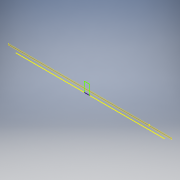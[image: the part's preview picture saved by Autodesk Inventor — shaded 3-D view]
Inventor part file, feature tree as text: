
AUTODESK INVENTOR PART (.ipt)
format: ipt  version: 2019 (Build 230136000, 136)  size: 148,480 bytes
history: native  units: mm
features: extrude x4, sketch x4, reference x4, other x4, fillet x2, plane x1, helix x1
ambient origin geometry x8: Origin, YZ Plane, XZ Plane, XY Plane, X Axis, Y Axis, Z Axis, Center Point
bodies: Solid1 (feature_tree)
feature tree (20):
  plane  "Work Plane1"
  extrude  "Extrusion1"  Depth=2.0mm
  fillet  "Fillet1"  Radius=6.2mm
  extrude  "Extrusion2"  Depth=4.0mm TaperAngle=0.0deg
  extrude  "Extrusion3"  Depth=4.0mm TaperAngle=0.0deg
  extrude  "Extrusion4"  [1 undecoded]
  fillet  "Fillet2"  [1 undecoded]
  sketch  "Sketch1"  dims[d0=4.0mm d1=0.0mm d2=2.0mm d3=6.2mm]
  reference  "Reference1"
  sketch  "Sketch2"  dims[d4=6.0mm d5=4.0mm d6=0.0mm]
  reference  "Reference2"
  sketch  "Sketch3"  dims[d7=4.0mm d8=0.0mm d9=4.0mm d10=0.0mm]
  reference  "Reference3"
  reference  "Reference4"
  sketch  "Sketch4"  dims[d11=2.0mm]
  other  "<userpath>\Documents\CAD Files\Helix DLP\Helix DLP.iam"
  helix  "Helix DLP.iam"  [1 undecoded]
  other  "30X30 - T-slot - Aluminium Profile:3"
  other  "30X30 - T-slot - Aluminium Profile:1"
  other  "Limit Switch (1):2"
note: 3 required parameter values undecoded (feature->parameter linkage not recoverable at this tier; creation-order binding heuristic only, values carry confidence <= 0.55)
